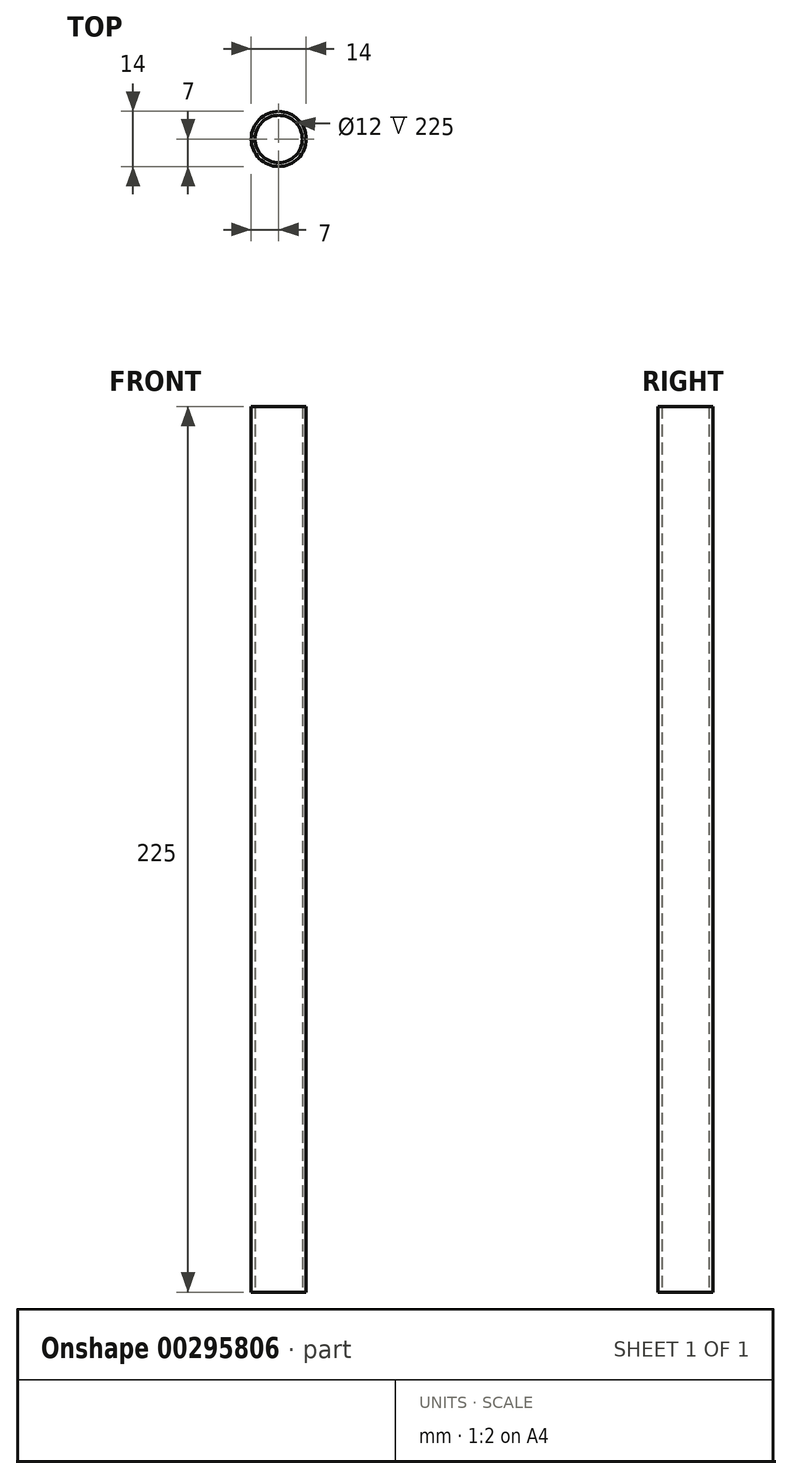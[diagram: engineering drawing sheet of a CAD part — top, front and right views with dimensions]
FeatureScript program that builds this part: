
annotation { "Feature Type Name" : "Feature", "Feature Type Description" : "" }
export const myFeature = defineFeature(function(context is Context, id is Id, definition is map)
    precondition{}
    {
        {
            var Q0;
            Q0=qCreatedBy(makeId("Top.planeOp"),FACE);
            var sketch = newSketch(context, id + "F0", { "sketchPlane" : qUnion([Q0])});
            skCircle(sketch, "E0", {"center": v(0, 0) * mm, "radius": 7 * mm});
            skCircle(sketch, "E1.0", {"center": v(0, 0) * mm, "radius": 6 * mm});
            skSolve(sketch);
        }
        {
            var Q0;
            Q0 = qSketchRegion(id + "F0", true);
            extrude(context, id + "F1", {"entities" : qUnion([Q0]), "depth" : 225 * mm});
        }
    });
